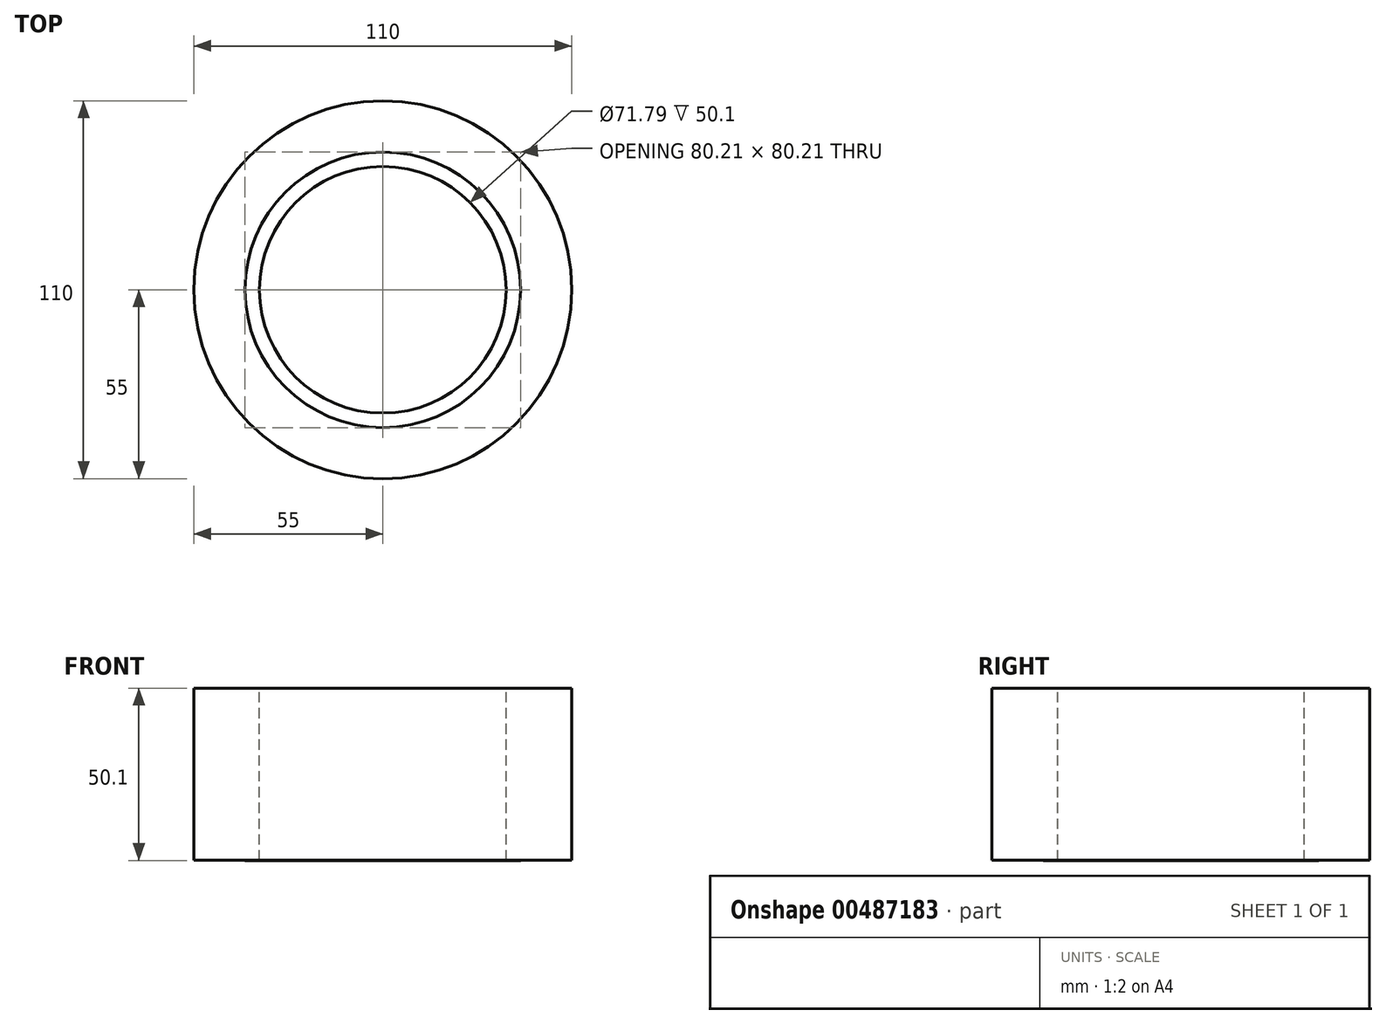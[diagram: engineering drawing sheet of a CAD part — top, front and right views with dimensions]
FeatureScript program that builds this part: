
annotation { "Feature Type Name" : "Feature", "Feature Type Description" : "" }
export const myFeature = defineFeature(function(context is Context, id is Id, definition is map)
    precondition{}
    {
        {
            var Q0;
            Q0=qCreatedBy(makeId("Front.planeOp"),FACE);
            var sketch = newSketch(context, id + "F0", { "sketchPlane" : qUnion([Q0])});
            skLineSegment(sketch, "E0", {"start": v(0, 25) * mm, "end": v(0, -25) * mm});
            skLineSegment(sketch, "E1.bottom", {"start": v(-55, 25) * mm, "end": v(-40, 25) * mm});
            skLineSegment(sketch, "E1.top", {"start": v(-55, -25) * mm, "end": v(-40, -25) * mm});
            skLineSegment(sketch, "E1.left", {"start": v(-55, 25) * mm, "end": v(-55, -25) * mm});
            skLineSegment(sketch, "E1.right", {"start": v(-40, 25) * mm, "end": v(-40, -25) * mm});
            skSolve(sketch);
        }
        {
            var Q0;
            Q0=qCreatedBy(makeId("Front.planeOp"),FACE);
            var sketch = newSketch(context, id + "F1", { "sketchPlane" : qUnion([Q0])});
            skLineSegment(sketch, "E2.bottom", {"start": v(-40.1, 25.04) * mm, "end": v(-35.9, 25.04) * mm});
            skLineSegment(sketch, "E2.top", {"start": v(-40.1, -25.06) * mm, "end": v(-35.9, -25.06) * mm});
            skLineSegment(sketch, "E2.left", {"start": v(-40.1, 25.04) * mm, "end": v(-40.1, -25.06) * mm});
            skLineSegment(sketch, "E2.right", {"start": v(-35.9, 25.04) * mm, "end": v(-35.9, -25.06) * mm});
            skSolve(sketch);
        }
        {
            var Q0;
            Q0=makeQuery(id+"F0.imprint","IMPRINT",FACE,{"disambiguationData":[TD([[makeQuery(id+"F0.imprint","IMPRINT",EDGE,{"derivedFrom":sQuery(id+"F0.wireOp",EDGE,"E1.bottom")}),-1.0]])]});
            var Q1;
            Q1=sQuery(id+"F0.wireOp",EDGE,"E0");
            revolve(context, id + "F2", {"entities" : qUnion([Q0]), "axis" : qUnion([Q1]), "revolveType" : RevolveType.FULL});
        }
        {
            var Q0;
            Q0=makeQuery(id+"F1.imprint","IMPRINT",FACE,{"disambiguationData":[TD([[makeQuery(id+"F1.imprint","IMPRINT",EDGE,{"derivedFrom":sQuery(id+"F1.wireOp",EDGE,"E2.bottom")}),-1.0]])]});
            var Q1;
            Q1=sQuery(id+"F0.wireOp",EDGE,"E0");
            revolve(context, id + "F3", {"operationType" : NewBodyOperationType.ADD, "entities" : qUnion([Q0]), "axis" : qUnion([Q1]), "revolveType" : RevolveType.FULL});
        }
    });
